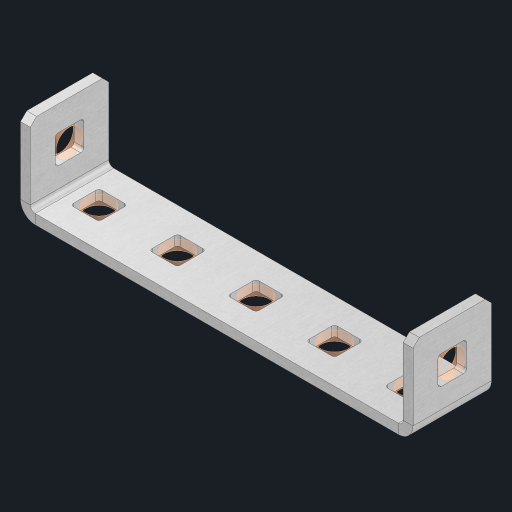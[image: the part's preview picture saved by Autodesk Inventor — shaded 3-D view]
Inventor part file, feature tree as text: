
AUTODESK INVENTOR PART (.ipt)
format: ipt  version: 2023 (Build 270158000, 158)  size: 413,184 bytes
history: native  units: in
note: dims shown in document units (in); Inventor stores cm internally (conversion verified against a paired STEP export)
features: other x12, sheet_metal_op x10, sketch x8, extrude x6, mirror x1, pattern_linear x1, chamfer x1
ambient origin geometry x8: Origin, YZ Plane, XZ Plane, XY Plane, X Axis, Y Axis, Z Axis, Center Point
bodies: Solid1 (feature_tree), Body (feature_tree)
feature tree (39):
  other  "Flange Pattern Plane"
  sheet_metal_op  "Flange Pattern"
  sheet_metal_op  "Body Pattern"
  other  "Arc Length"
  mirror  "Notch Mirror"
  pattern_linear  "Notch Pattern"  Spacing1=0.25in  [1 undecoded]
  chamfer  "End Chamfer"
  extrude  "Half Cut"  Depth=0.0625in
  sketch  "Sketch1"  dims[d0=2.5in]
  other  "Plate1"
  sketch  "Sketch2"  dims[d1=0.5in]
  other  "Plate2"
  sheet_metal_op  "Bend1"
  sheet_metal_op  "Corner1"
  sketch  "Sketch3"  dims[d2=0.0625in]
  other  "Flange Pattern Sketch"
  sketch  "Sketch7"  dims[d3=0.0625in]
  other  "Srf1"
  other  "Srf2"
  sketch  "Sketch8"  dims[d4=0.0312in]
  sketch  "Sketch9"  dims[d5=0.125in]
  other  "Srf91"
  sheet_metal_op  "Body Pattern Sketch"
  other  "Srf92"
  sketch  "Sketch13"  dims[d6=0.0625in]
  sketch  "Sketch14"  dims[d7=0.5in d8=90.0deg d9=0.0312in d10=0.25in d11=0.0625in d12=0.0625in d16=0.182in d17=0.02in d18=0.0625in d19=0.0in d20=0.25in d21=0.25in d46=0.172in d47=1.0in d48=0.0in d49=0.182in d50=0.02in d51=0.25in d52=0.25in d53=0.0625in d54=0.0in d55=0.172in d56=1.0in d57=0.0in d60=0.3937in d62=0.5in d63=1.9685in d65=0.5in d85=0.1473in d86=0.1782in d88=0.04in d89=0.0625in d90=0.0in d91=0.04in d92=0.0491in d95=2.5in d96=0.04in d97=0.25in d98=45.0deg d101=0.0in d102=2.497in d131=2.5in d132=0.3937in d134=0.5in]
  other  "Srf856"
  other  "Srf1376"
  other  "Srf1377"
  sheet_metal_op  "Flange Stamp"
  sheet_metal_op  "Flange Circle"
  sheet_metal_op  "Body Stamp"
  sheet_metal_op  "Body Circle"
  sheet_metal_op  "Notch"
  extrude  "ExtrusionSrf2"  Depth=0.0625in
  extrude  "ExtrusionSrf92"  Depth=0.182in
  extrude  "ExtrusionSrf856"  Depth=0.02in
  extrude  "ExtrusionSrf1376"  Depth=0.0625in
  extrude  "ExtrusionSrf1377"  TaperAngle=0.0deg  [1 undecoded]
note: 2 required parameter values undecoded (feature->parameter linkage not recoverable at this tier; creation-order binding heuristic only, values carry confidence <= 0.55)
